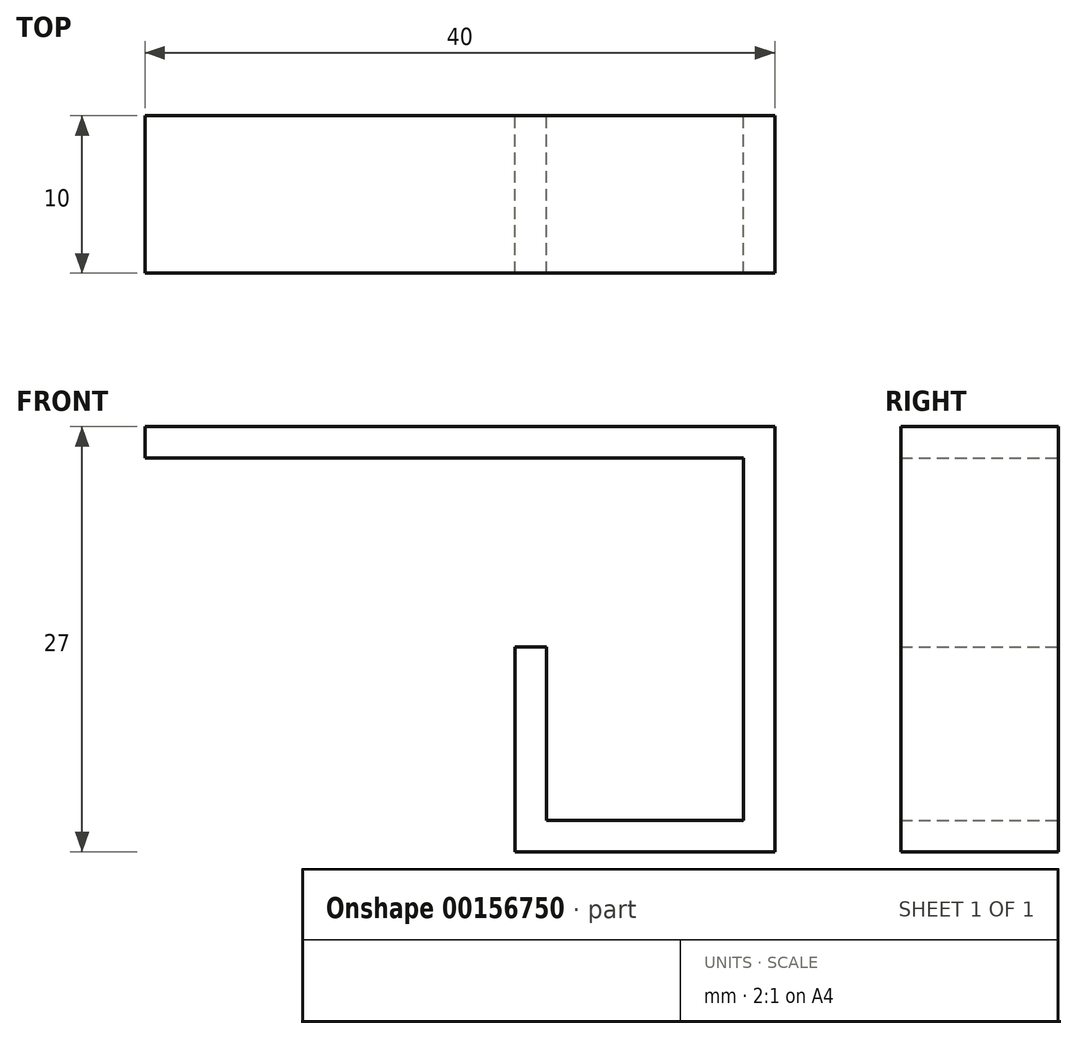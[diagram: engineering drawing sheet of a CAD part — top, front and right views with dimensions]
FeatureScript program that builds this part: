
annotation { "Feature Type Name" : "Feature", "Feature Type Description" : "" }
export const myFeature = defineFeature(function(context is Context, id is Id, definition is map)
    precondition{}
    {
        {
            var Q0;
            Q0=qCreatedBy(makeId("Front.planeOp"),FACE);
            var sketch = newSketch(context, id + "F0", { "sketchPlane" : qUnion([Q0])});
            skLineSegment(sketch, "E0.top", {"start": v(-9.85, -17.5) * mm, "end": v(30.15, -17.5) * mm});
            skLineSegment(sketch, "E0.left", {"start": v(-9.85, 9.5) * mm, "end": v(-9.85, -17.5) * mm});
            skLineSegment(sketch, "E0.right", {"start": v(30.15, 9.5) * mm, "end": v(30.15, -17.5) * mm});
            skLineSegment(sketch, "E1", {"start": v(-9.85, 9.5) * mm, "end": v(-9.85, 7.5) * mm});
            skLineSegment(sketch, "E2", {"start": v(-9.85, 7.5) * mm, "end": v(28.15, 7.5) * mm});
            skLineSegment(sketch, "E3", {"start": v(28.15, 7.5) * mm, "end": v(28.15, -15.5) * mm});
            skLineSegment(sketch, "E4", {"start": v(28.15, -15.5) * mm, "end": v(15.65, -15.5) * mm});
            skLineSegment(sketch, "E5", {"start": v(15.65, -15.5) * mm, "end": v(15.65, -4.5) * mm});
            skLineSegment(sketch, "E6", {"start": v(15.65, -4.5) * mm, "end": v(13.65, -4.5) * mm});
            skLineSegment(sketch, "E7", {"start": v(13.65, -4.5) * mm, "end": v(13.65, -17.5) * mm});
            skPoint(sketch, "E8.orphan", {"position": v(28.15, 9.5) * mm});
            skLineSegment(sketch, "E9", {"start": v(-9.85, 9.5) * mm, "end": v(30.15, 9.5) * mm});
            skLineSegment(sketch, "E10", {"start": v(15.65, 0) * mm, "end": v(28.15, 0) * mm});
            skPoint(sketch, "E10.endSnap0", {"position": v(28.15, -4) * mm});
            skLineSegment(sketch, "E11", {"start": v(28.15, 0) * mm, "end": v(28.15, 3.5) * mm});
            skLineSegment(sketch, "E12", {"start": v(28.15, 3.5) * mm, "end": v(15.65, 3.5) * mm});
            skLineSegment(sketch, "E13", {"start": v(15.65, 3.5) * mm, "end": v(15.65, 0) * mm});
            skCircle(sketch, "E14", {"center": v(10.15, -3.5) * mm, "radius": 2.5 * mm});
            skSolve(sketch);
        }
        {
            var Q0;
            {var subQ5=sQuery(id+"F0.wireOp",EDGE,"E0.right");Q0=makeQuery(id+"F0.imprint","IMPRINT",FACE,{"disambiguationData":[TD([[makeQuery(id+"F0.imprint","IMPRINT",EDGE,{"derivedFrom":subQ5}),-1.0]])]});}
            extrude(context, id + "F1", {"entities" : qUnion([Q0]), "depth" : 10 * mm});
        }
        {
            var Q0;
            {var subQ0=sQuery(id+"F0.wireOp",EDGE,"E0.left");Q0=makeQuery(id+"F0.imprint","IMPRINT",FACE,{"disambiguationData":[TD([[makeQuery(id+"F0.imprint","IMPRINT",EDGE,{"derivedFrom":subQ0}),1.0]])]});}
            extrude(context, id + "F2", {"entities" : qUnion([Q0]), "operationType" : NewBodyOperationType.ADD, "depth" : 3 * mm});
        }
    });
